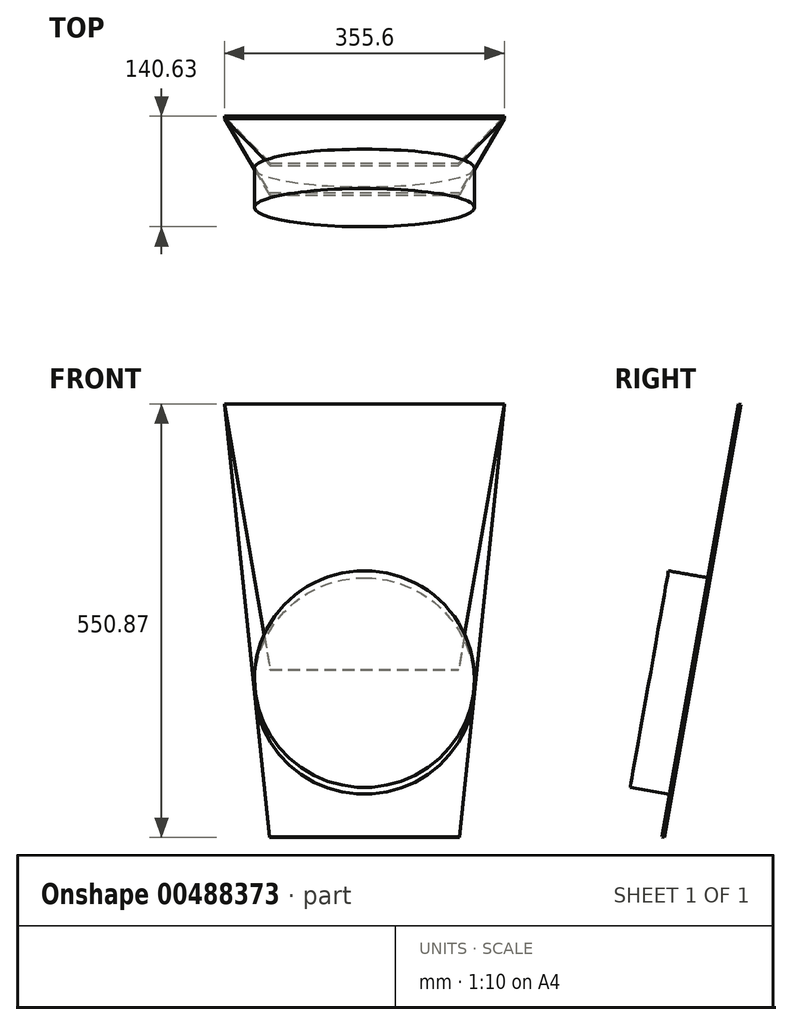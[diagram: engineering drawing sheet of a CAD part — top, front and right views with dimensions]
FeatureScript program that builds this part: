
annotation { "Feature Type Name" : "Feature", "Feature Type Description" : "" }
export const myFeature = defineFeature(function(context is Context, id is Id, definition is map)
    precondition{}
    {
        {
            var Q0;
            Q0=qCreatedBy(makeId("Right.planeOp"),FACE);
            var sketch = newSketch(context, id + "F0", { "sketchPlane" : qUnion([Q0])});
            skLineSegment(sketch, "E0.bottom", {"start": v(-63.44, 77.4) * mm, "end": v(11.6, 64.17) * mm});
            skLineSegment(sketch, "E0.top", {"start": v(33.6, 627.7) * mm, "end": v(108.64, 614.48) * mm});
            skLineSegment(sketch, "E0.left", {"start": v(-63.44, 77.4) * mm, "end": v(33.6, 627.7) * mm});
            skLineSegment(sketch, "E0.right", {"start": v(11.6, 64.17) * mm, "end": v(108.64, 614.48) * mm});
            skLineSegment(sketch, "E1.bottom", {"start": v(103.65, 38.1) * mm, "end": v(510.05, 38.1) * mm});
            skLineSegment(sketch, "E1.top", {"start": v(103.65, 546.1) * mm, "end": v(510.05, 546.1) * mm});
            skLineSegment(sketch, "E1.left", {"start": v(103.65, 38.1) * mm, "end": v(103.65, 546.1) * mm});
            skLineSegment(sketch, "E1.right", {"start": v(510.05, 38.1) * mm, "end": v(510.05, 546.1) * mm});
            skLineSegment(sketch, "E2.bottom", {"start": v(42.48, 128.48) * mm, "end": v(86.93, 128.48) * mm});
            skLineSegment(sketch, "E2.top", {"start": v(42.48, 84.03) * mm, "end": v(86.93, 84.03) * mm});
            skLineSegment(sketch, "E2.left", {"start": v(42.48, 128.48) * mm, "end": v(42.48, 84.03) * mm});
            skLineSegment(sketch, "E2.right", {"start": v(86.93, 128.48) * mm, "end": v(86.93, 84.03) * mm});
            skPoint(sketch, "E2.middle", {"position": v(64.7, 106.26) * mm});
            skSolve(sketch);
        }
        {
            var Q0;
            Q0=qCreatedBy(makeId("Top.planeOp"),FACE);
            var sketch = newSketch(context, id + "F1", { "sketchPlane" : qUnion([Q0])});
            skLineSegment(sketch, "E3", {"start": v(-119.23, 0) * mm, "end": v(152.83, 0) * mm});
            skSolve(sketch);
        }
        {
            var Q0;
            Q0=qCreatedBy(makeId("Front.planeOp"),FACE);
            var Q1;
            Q1=sQuery(id+"F1.wireOp",EDGE,"E3");
            cPlane(context, id + "F2", {"entities" : qUnion([Q0, Q1]), "cplaneType" : CPlaneType.LINE_ANGLE, "offset" : 25.4 * mm, "angle" : 10 * degree, "oppositeDirection" : true, "width" : 152.4 * mm, "height" : 152.4 * mm});
        }
        {
            var Q0;
            Q0=qCreatedBy(id+"F2.planeOp",FACE);
            var sketch = newSketch(context, id + "F3", { "sketchPlane" : qUnion([Q0])});
            skLineSegment(sketch, "E4.bottom", {"start": v(177.8, 622.3) * mm, "end": v(-177.8, 622.3) * mm});
            skLineSegment(sketch, "E4.top", {"start": v(120.72, 63.5) * mm, "end": v(-120.72, 63.5) * mm});
            skPoint(sketch, "E5", {"position": v(0, 63.5) * mm});
            skCircle(sketch, "E6", {"center": v(0, 258.26) * mm, "radius": 139.7 * mm, "construction": true});
            skCircle(sketch, "E7", {"center": v(0, 330.2) * mm, "radius": 17.46 * mm, "construction": true});
            skPoint(sketch, "E8", {"position": v(0, 622.3) * mm});
            skLineSegment(sketch, "E9", {"start": v(177.8, 622.3) * mm, "end": v(120.72, 63.5) * mm});
            skLineSegment(sketch, "E10", {"start": v(-177.8, 622.3) * mm, "end": v(-120.72, 63.5) * mm});
            skSolve(sketch);
        }
        {
            var Q0;
            Q0 = qSketchRegion(id + "F3", true);
            extrude(context, id + "F4", {"entities" : qUnion([Q0]), "depth" : 3.17 * mm});
        }
        {
            var Q0;
            Q0=qCreatedBy(id+"F2.planeOp",FACE);
            var sketch = newSketch(context, id + "F5", { "sketchPlane" : qUnion([Q0])});
            skCircle(sketch, "E11", {"center": v(0, 422.1) * mm, "radius": 139.7 * mm, "construction": true});
            skLineSegment(sketch, "E12.0", {"start": v(177.8, 622.3) * mm, "end": v(-177.8, 622.3) * mm});
            skLineSegment(sketch, "E13", {"start": v(177.8, 622.3) * mm, "end": v(119.76, 279.4) * mm});
            skLineSegment(sketch, "E14", {"start": v(-177.8, 622.3) * mm, "end": v(-119.76, 279.4) * mm});
            skLineSegment(sketch, "E15", {"start": v(119.76, 279.4) * mm, "end": v(-119.76, 279.4) * mm});
            skSolve(sketch);
        }
        {
            var Q0;
            Q0 = qSketchRegion(id + "F5", true);
            extrude(context, id + "F6", {"entities" : qUnion([Q0]), "depth" : 3.17 * mm});
        }
        {
            var Q0;
            Q0=makeQuery(id+"F3.imprint","IMPRINT",FACE,{"disambiguationData":[TD([[makeQuery(id+"F3.imprint","IMPRINT",EDGE,{"derivedFrom":sQuery(id+"F3.wireOp",EDGE,"E4.bottom")}),1.0]])]});
            var sketch = newSketch(context, id + "F7", { "sketchPlane" : qUnion([Q0])});
            skCircle(sketch, "E16.0", {"center": v(0, 258.26) * mm, "radius": 139.7 * mm});
            skSolve(sketch);
        }
        {
            var Q0;
            Q0 = qSketchRegion(id + "F7", true);
            extrude(context, id + "F8", {"entities" : qUnion([Q0]), "oppositeDirection" : true, "depth" : 50.8 * mm});
        }
    });
